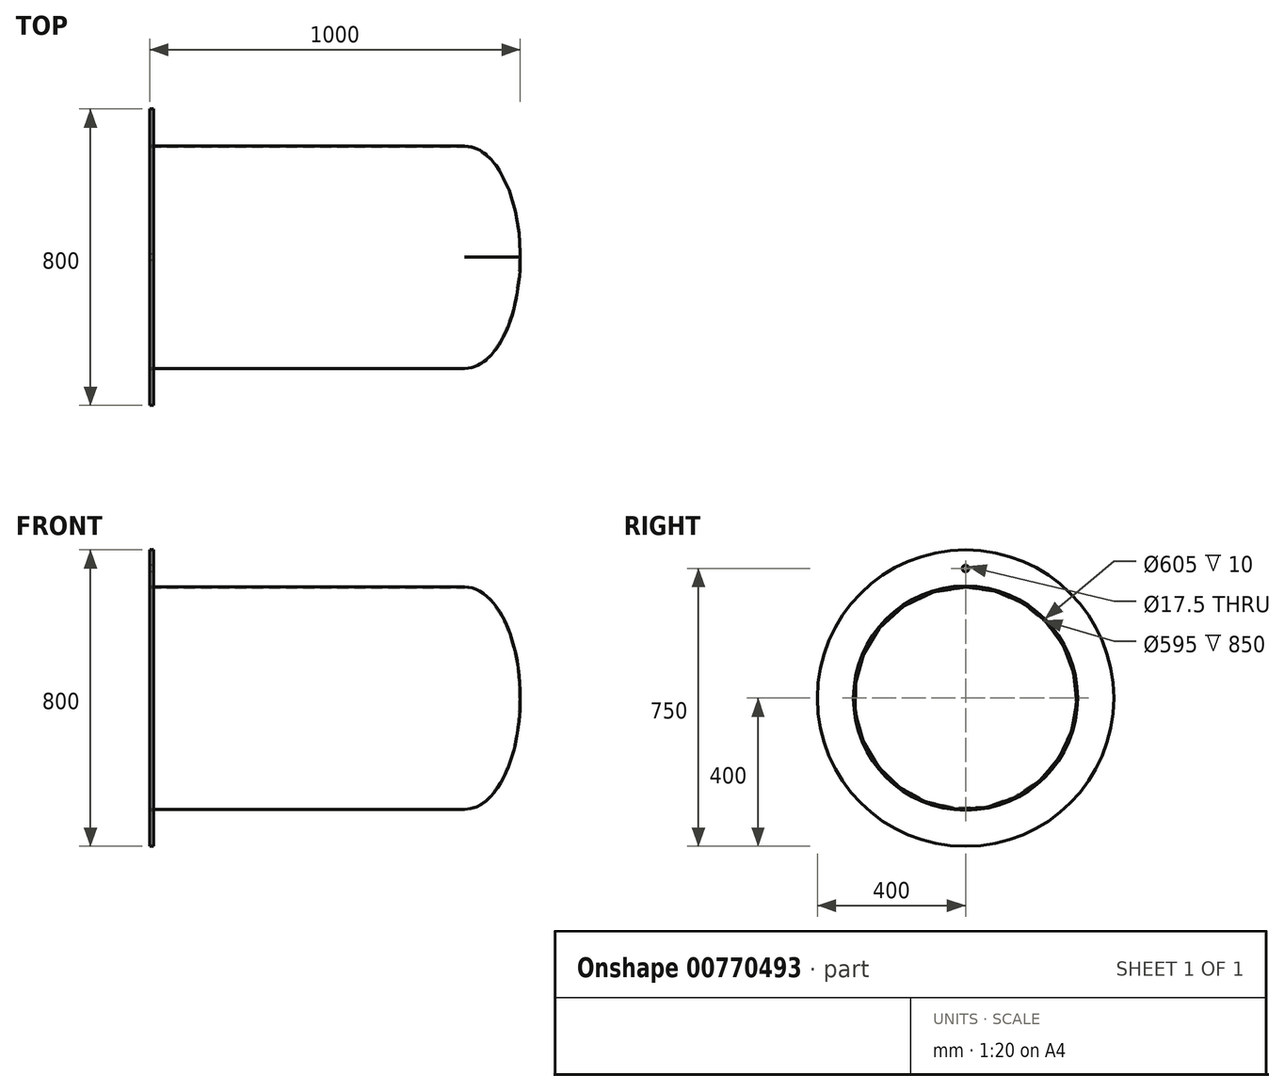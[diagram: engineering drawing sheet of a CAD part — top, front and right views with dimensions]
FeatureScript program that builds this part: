
annotation { "Feature Type Name" : "Feature", "Feature Type Description" : "" }
export const myFeature = defineFeature(function(context is Context, id is Id, definition is map)
    precondition{}
    {
        {
            var Q0;
            Q0=qCreatedBy(makeId("Front.planeOp"),FACE);
            var sketch = newSketch(context, id + "F0", { "sketchPlane" : qUnion([Q0])});
            skLineSegment(sketch, "E0", {"start": v(0, 0) * mm, "end": v(0, 300) * mm});
            skLineSegment(sketch, "E1", {"start": v(0, 300) * mm, "end": v(850, 300) * mm});
            skLineSegment(sketch, "E2", {"start": v(0, 0) * mm, "end": v(1000, 0) * mm});
            skLineSegment(sketch, "E3", {"start": v(0, 0) * mm, "end": v(-480.81, 0) * mm, "construction": true});
            skEllipticalArc(sketch, "E4", {});
            const initialGuessF0  = {"E4": [0.85, 0, 0, 1, 0.3, 0.15, 4.71238898038469, 0]};
            skSetInitialGuess(sketch, initialGuessF0);
            skSolve(sketch);
        }
        {
            var Q0;
            Q0=makeQuery(id+"F0.imprint","IMPRINT",FACE,{"disambiguationData":[TD([[makeQuery(id+"F0.imprint","IMPRINT",EDGE,{"derivedFrom":sQuery(id+"F0.wireOp",EDGE,"E0")}),-1.0]])]});
            var Q1;
            Q1=sQuery(id+"F0.wireOp",EDGE,"E3");
            revolve(context, id + "F1", {"surfaceOperationType" : NewSurfaceOperationType.NEW, "entities" : qUnion([Q0]), "axis" : qUnion([Q1]), "revolveType" : RevolveType.FULL});
        }
        {
            var Q0;
            Q0=makeQuery(id+"F1.opRevolve","SWEPT_FACE",FACE,{"disambiguationData":[OSD([sQuery(id+"F0.wireOp",EDGE,"E0")])]});
            var Q1;
            Q1=makeQuery(id+"F1.opRevolve","SWEPT_BODY",BODY,{"disambiguationData":[OSD([sQuery(id+"F0.wireOp",EDGE,"E0"),sQuery(id+"F0.wireOp",EDGE,"E1"),sQuery(id+"F0.wireOp",EDGE,"E2"),sQuery(id+"F0.wireOp",EDGE,"E4")])]});
            shell(context, id + "F2", {"entities" : qUnion([Q0]), "parts" : qUnion([Q1]), "thickness" : 2.5 * mm});
        }
        {
            var Q0;
            Q0=qCreatedBy(makeId("Front.planeOp"),FACE);
            var sketch = newSketch(context, id + "F3", { "sketchPlane" : qUnion([Q0])});
            skLineSegment(sketch, "E5.bottom", {"start": v(0, 302.5) * mm, "end": v(10, 302.5) * mm});
            skLineSegment(sketch, "E5.top", {"start": v(0, 400) * mm, "end": v(10, 400) * mm});
            skLineSegment(sketch, "E5.left", {"start": v(0, 302.5) * mm, "end": v(0, 400) * mm});
            skLineSegment(sketch, "E5.right", {"start": v(10, 302.5) * mm, "end": v(10, 400) * mm});
            skLineSegment(sketch, "E6", {"start": v(0, 0) * mm, "end": v(-80.39, 0) * mm, "construction": true});
            skSolve(sketch);
        }
        {
            var Q0;
            Q0=makeQuery(id+"F3.imprint","IMPRINT",FACE,{"disambiguationData":[TD([[makeQuery(id+"F3.imprint","IMPRINT",EDGE,{"derivedFrom":sQuery(id+"F3.wireOp",EDGE,"E5.bottom")}),1.0]])]});
            var Q1;
            Q1=sQuery(id+"F3.wireOp",EDGE,"E6");
            revolve(context, id + "F4", {"surfaceOperationType" : NewSurfaceOperationType.NEW, "entities" : qUnion([Q0]), "axis" : qUnion([Q1]), "revolveType" : RevolveType.FULL});
        }
        {
            var Q0;
            Q0=makeQuery(id+"F4.opRevolve","SWEPT_FACE",FACE,{"disambiguationData":[OSD([sQuery(id+"F3.wireOp",EDGE,"E5.left")])]});
            var sketch = newSketch(context, id + "F5", { "sketchPlane" : qUnion([Q0])});
            skCircle(sketch, "E7", {"center": v(0, 0) * mm, "radius": 350 * mm, "construction": true});
            skPoint(sketch, "E8", {"position": v(0, 350) * mm});
            skSolve(sketch);
        }
        {
            var Q0;
            Q0=sQuery(id+"F5.wireOp",VERTEX,"E8");
            var Q1;
            Q1=makeQuery(id+"F4.opRevolve","SWEPT_BODY",BODY,{"disambiguationData":[OSD([sQuery(id+"F3.wireOp",EDGE,"E5.bottom"),sQuery(id+"F3.wireOp",EDGE,"E5.top"),sQuery(id+"F3.wireOp",EDGE,"E5.left"),sQuery(id+"F3.wireOp",EDGE,"E5.right")])]});
            hole(context, id + "F6", {"style" : HoleStyle.SIMPLE, "endStyle" : HoleEndStyle.THROUGH, "standardTappedOrClearance" : lookupTablePath({ "standard" : "ISO", "fit" : "Normal", "size" : "M16", "type" : "Clearance" }), "standardBlindInLast" : lookupTablePath({ "fit" : "Standard", "standard" : "ISO", "size" : "M16", "type" : "Clearance" }), "holeDiameter" : 17.5 * mm, "majorDiameter" : 5 * mm, "isTappedThrough" : true, "tappedDepth" : 12 * mm, "tapClearance" : 3, "locations" : qUnion([Q0]), "scope" : qUnion([Q1])});
        }
    });
